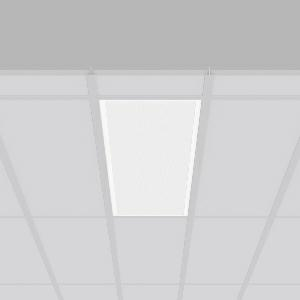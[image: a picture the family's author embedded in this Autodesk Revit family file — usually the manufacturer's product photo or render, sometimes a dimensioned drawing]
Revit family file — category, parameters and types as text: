
# Revit family: sidelite_eco_672369_002_1_04_2fb2
name_source: partatom
category: Lighting Fixtures
units: mm (PartAtom-declared; Revit-internal decimal feet)

## family parameters
Cut with Voids When Loaded = No
Host = Face
Light Source = No
Part Type = Normal
Room Calculation Point = No
Round Connector Dimension = Use Diameter
Shared = No

## types (1)
- SIDELITE ECO (1 x LED Modul 840, 3450 lm, 4000)
    Apparent Load = 29 VA
    CIE Flux Codes = 59 87 97 100 100
    Color Rendering = 80
    Color Temperature = 4000
    Default Elevation = 1800 mm
    Description = Series: SIDELITE ECO
Highly economical recessed luminaire with progressive LED technology. For escape route illumination. Frame made of aluminium, powder-coated. Diffuser plastic microprismatic. Lightguide and diffuser made of non-yellowing plastic (PMMA). Lateral light emission (RZB SIDELITE technology) for homogeneous light distribution. External driver. Self-contained system with automatic self-test and feedback to the RZB monitoring system MULTIDIGIT. External driver with simple plug-in locking system. Extended connection cable (1.90 m). 
Colour: white
Length: 1195 mm
Width: 295 mm
Cut-out length: 1170 mm
Cut-out width: 270 mm
Recess height: 160 mm
Luminaire: recess height: 40 mm
Weight: 4.4 kg
Operating mode: maintained power mode
Duration time: 8 h
Lamp: LED
Socket: without socket
Colour temperature: 4000K
Colour rendering index (CRI): 80
System power: 29 W
Rated luminous flux: 3450 lm
Luminous flux, emergency: 240 lm
System power, emergency: -
Control gear: Regulated power supply
Protection class: I
Type of protection: IP 40
    Height = 0 mm  [stored 0 ft]
    Lamp = 1 x LED Modul 840
    Lamp Light Flux = 3450 lm
    Lamp count = 1
    Length = 1195 mm
    Lifetime = 50000 h
    Luminous efficacy = 119 lm/W
    Manufacturer = RZB
    ModVariant = No
    Model = 672369.002.1.04
    Mounting Place = Ceiling
    Mounting Type = Recessed
    Number of Poles = 1
    OnlyDefault = Yes
    Power Factor = 1
    Product Name = SIDELITE ECO
    Product group = Recessed modular luminaires
    ProductGroupID = 406
    Protection Class = Protection class I
    Protection Degree = IP 40
    RLX_Detail_Level = 1
    RLX_Emergency_Light_Flux = 240 lm
    RLX_Emergency_Type = 3
    RLX_Emergency_Type_DB = Yes
    RlxData = <blob elided: 34849 chars, md5=6c39617f>
    Socket = socket
    Standby Power = 0 W
    System Light Flux = 3450 lm
    System Power = 29 W
    Type Comments = Product without accessories
    Type Image = 312366.002.jpg
    URL = http://relux.com
    VarID = ---
    Voltage = 230 V
    Voltage Range = 220-240 V
    Weight = 0.00 kg
    Width = 295 mm

note: [stored X ft] marks values corroborated as IEEE doubles in the binary element streams (Revit-internal decimal feet)

## geometry (parser evidence)
native form markers: Blend x4, Sweep x10
no freeform markers — native parametric forms only
